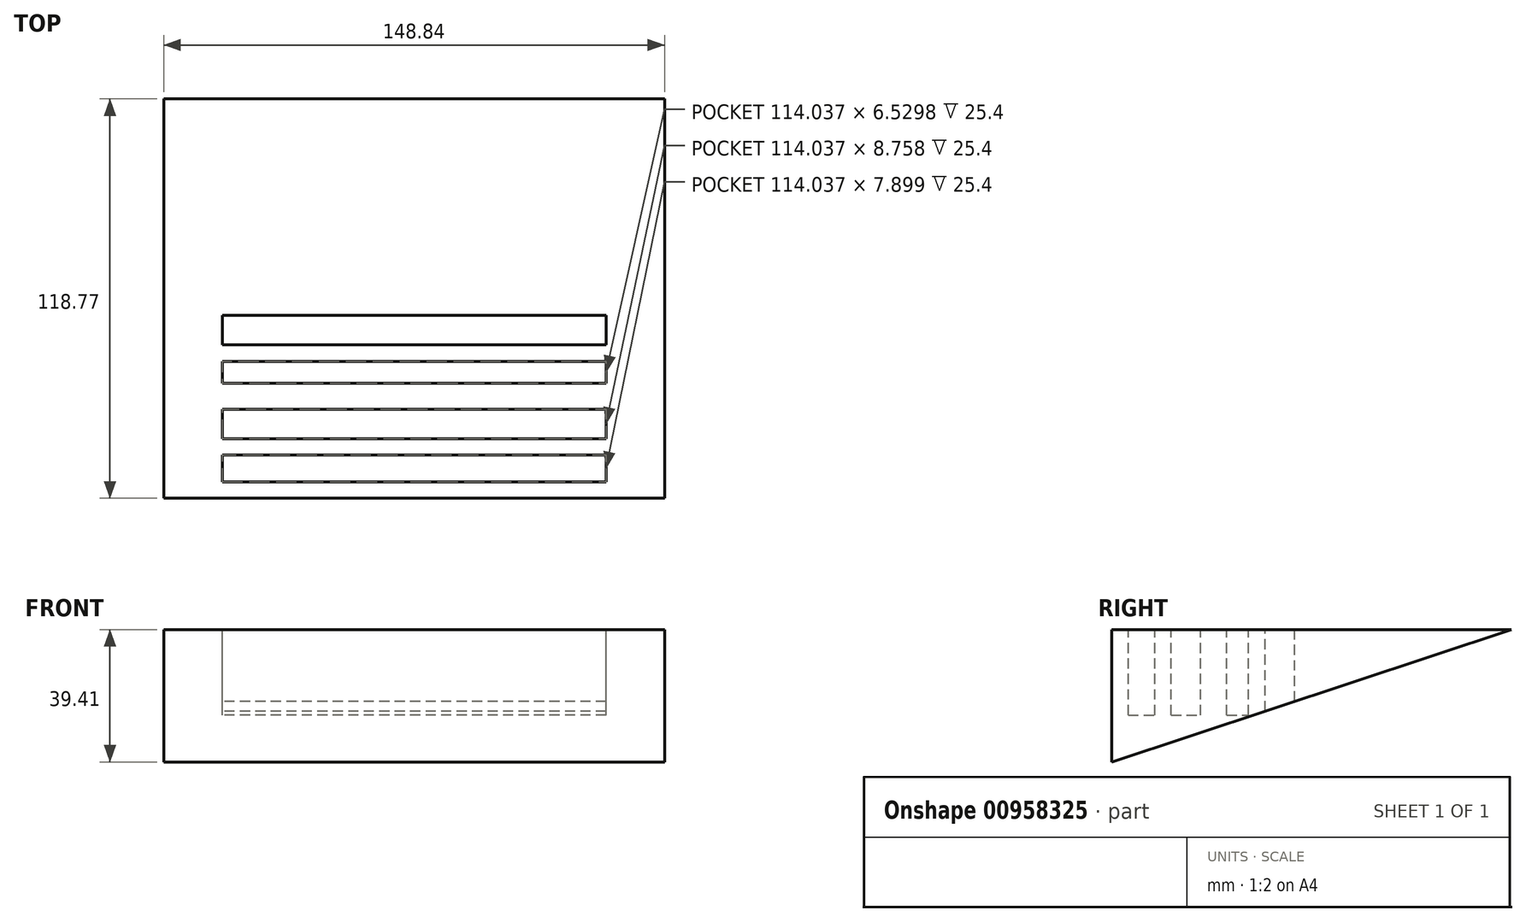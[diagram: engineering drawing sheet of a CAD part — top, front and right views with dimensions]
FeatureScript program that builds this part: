
annotation { "Feature Type Name" : "Feature", "Feature Type Description" : "" }
export const myFeature = defineFeature(function(context is Context, id is Id, definition is map)
    precondition{}
    {
        {
            var Q0;
            Q0=qCreatedBy(makeId("Top.planeOp"),FACE);
            var sketch = newSketch(context, id + "F0", { "sketchPlane" : qUnion([Q0])});
            skLineSegment(sketch, "E0.bottom", {"start": v(76.73, -42.04) * mm, "end": v(-76.73, -42.04) * mm});
            skLineSegment(sketch, "E0.top", {"start": v(76.73, 42.04) * mm, "end": v(-76.73, 42.04) * mm});
            skLineSegment(sketch, "E0.left", {"start": v(76.73, -42.04) * mm, "end": v(76.73, 42.04) * mm});
            skLineSegment(sketch, "E0.right", {"start": v(-76.73, -42.04) * mm, "end": v(-76.73, 42.04) * mm});
            skPoint(sketch, "E0.middle", {"position": v(0, 0) * mm});
            skLineSegment(sketch, "E1.bottom", {"start": v(57.02, -30.56) * mm, "end": v(-57.02, -30.56) * mm});
            skLineSegment(sketch, "E1.top", {"start": v(57.02, -21.8) * mm, "end": v(-57.02, -21.8) * mm});
            skLineSegment(sketch, "E1.left", {"start": v(57.02, -30.56) * mm, "end": v(57.02, -21.8) * mm});
            skLineSegment(sketch, "E1.right", {"start": v(-57.02, -30.56) * mm, "end": v(-57.02, -21.8) * mm});
            skPoint(sketch, "E1.middle", {"position": v(0, -26.19) * mm});
            skLineSegment(sketch, "E2.bottom", {"start": v(57.02, -44.38) * mm, "end": v(-57.02, -44.38) * mm});
            skLineSegment(sketch, "E2.top", {"start": v(57.02, -35.51) * mm, "end": v(-57.02, -35.51) * mm});
            skLineSegment(sketch, "E2.left", {"start": v(57.02, -44.38) * mm, "end": v(57.02, -35.51) * mm});
            skLineSegment(sketch, "E2.right", {"start": v(-57.02, -44.38) * mm, "end": v(-57.02, -35.51) * mm});
            skPoint(sketch, "E2.middle", {"position": v(0, -39.95) * mm});
            skLineSegment(sketch, "E3.bottom", {"start": v(57.02, -58.51) * mm, "end": v(-57.02, -58.51) * mm});
            skLineSegment(sketch, "E3.top", {"start": v(57.02, -49.76) * mm, "end": v(-57.02, -49.76) * mm});
            skLineSegment(sketch, "E3.left", {"start": v(57.02, -58.51) * mm, "end": v(57.02, -49.76) * mm});
            skLineSegment(sketch, "E3.right", {"start": v(-57.02, -58.51) * mm, "end": v(-57.02, -49.76) * mm});
            skPoint(sketch, "E3.middle", {"position": v(0, -54.14) * mm});
            skLineSegment(sketch, "E4.bottom", {"start": v(57.02, -71.27) * mm, "end": v(-57.02, -71.27) * mm});
            skLineSegment(sketch, "E4.top", {"start": v(57.02, -63.37) * mm, "end": v(-57.02, -63.37) * mm});
            skLineSegment(sketch, "E4.left", {"start": v(57.02, -71.27) * mm, "end": v(57.02, -63.37) * mm});
            skLineSegment(sketch, "E4.right", {"start": v(-57.02, -71.27) * mm, "end": v(-57.02, -63.37) * mm});
            skPoint(sketch, "E4.middle", {"position": v(0, -67.32) * mm});
            skSolve(sketch);
        }
        {
            var Q0;
            Q0=qCreatedBy(makeId("Right.planeOp"),FACE);
            var sketch = newSketch(context, id + "F1", { "sketchPlane" : qUnion([Q0])});
            skLineSegment(sketch, "E5", {"start": v(-76.2, 0) * mm, "end": v(-76.2, -39.41) * mm});
            skLineSegment(sketch, "E6", {"start": v(-76.2, -39.41) * mm, "end": v(42.57, 0) * mm});
            skLineSegment(sketch, "E7", {"start": v(-76.2, 0) * mm, "end": v(42.57, 0) * mm});
            skSolve(sketch);
        }
        {
            var Q0;
            Q0=makeQuery(id+"F1.imprint","IMPRINT",FACE,{"disambiguationData":[TD([[makeQuery(id+"F1.imprint","IMPRINT",EDGE,{"derivedFrom":sQuery(id+"F1.wireOp",EDGE,"E5")}),1.0]])]});
            extrude(context, id + "F2", {"entities" : qUnion([Q0]), "endBound" : BoundingType.SYMMETRIC, "depth" : 148.84 * mm, "offsetDistance" : 25.4 * mm});
        }
        {
            var Q0;
            Q0=makeQuery(id+"F0.imprint","IMPRINT",FACE,{"disambiguationData":[TD([[makeQuery(id+"F0.imprint","IMPRINT",EDGE,{"derivedFrom":sQuery(id+"F0.wireOp",EDGE,"E1.bottom")}),-1.0]])]});
            extrude(context, id + "F3", {"entities" : qUnion([Q0]), "operationType" : NewBodyOperationType.REMOVE, "oppositeDirection" : true, "depth" : 25.4 * mm, "offsetDistance" : 25.4 * mm});
        }
        {
            var Q0;
            {var subQ5=sQuery(id+"F0.wireOp",EDGE,"E2.top");Q0=makeQuery(id+"F0.imprint","IMPRINT",FACE,{"disambiguationData":[TD([[makeQuery(id+"F0.imprint","IMPRINT",EDGE,{"derivedFrom":subQ5}),1.0]])]});}
            extrude(context, id + "F4", {"entities" : qUnion([Q0]), "operationType" : NewBodyOperationType.REMOVE, "oppositeDirection" : true, "depth" : 25.4 * mm, "offsetDistance" : 25.4 * mm});
        }
        {
            var Q0;
            Q0=makeQuery(id+"F0.imprint","IMPRINT",FACE,{"disambiguationData":[TD([[makeQuery(id+"F0.imprint","IMPRINT",EDGE,{"derivedFrom":sQuery(id+"F0.wireOp",EDGE,"E3.bottom")}),-1.0]])]});
            extrude(context, id + "F5", {"entities" : qUnion([Q0]), "operationType" : NewBodyOperationType.REMOVE, "oppositeDirection" : true, "depth" : 25.4 * mm, "offsetDistance" : 25.4 * mm});
        }
        {
            var Q0;
            Q0=makeQuery(id+"F0.imprint","IMPRINT",FACE,{"disambiguationData":[TD([[makeQuery(id+"F0.imprint","IMPRINT",EDGE,{"derivedFrom":sQuery(id+"F0.wireOp",EDGE,"E4.bottom")}),-1.0]])]});
            extrude(context, id + "F6", {"entities" : qUnion([Q0]), "operationType" : NewBodyOperationType.REMOVE, "oppositeDirection" : true, "depth" : 25.4 * mm, "offsetDistance" : 25.4 * mm});
        }
    });
